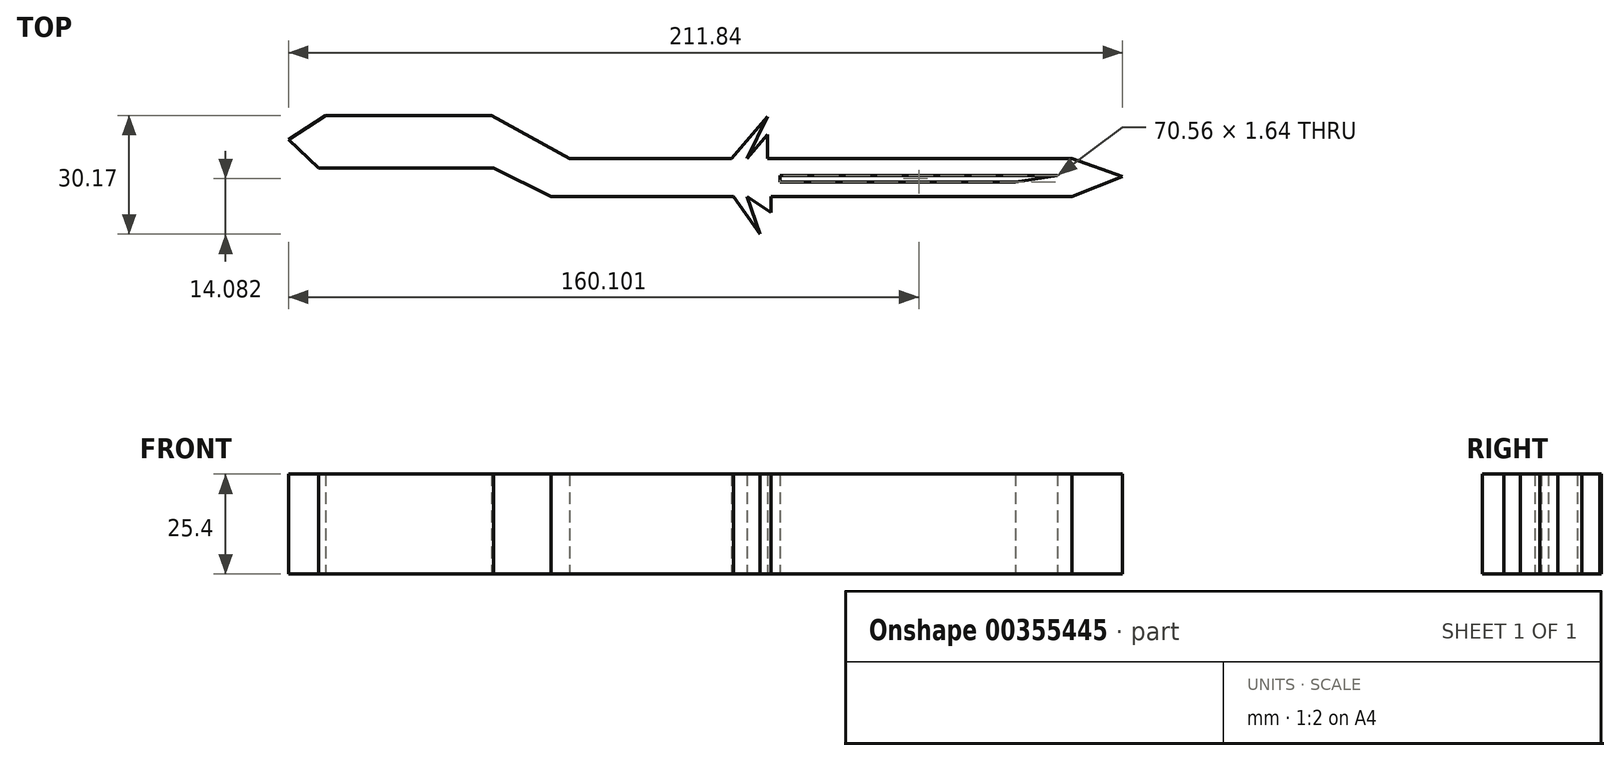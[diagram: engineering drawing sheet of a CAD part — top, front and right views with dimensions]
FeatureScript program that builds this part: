
annotation { "Feature Type Name" : "Feature", "Feature Type Description" : "" }
export const myFeature = defineFeature(function(context is Context, id is Id, definition is map)
    precondition{}
    {
        {
            var Q0;
            Q0=qCreatedBy(makeId("Top.planeOp"),FACE);
            var sketch = newSketch(context, id + "F0", { "sketchPlane" : qUnion([Q0])});
            skLineSegment(sketch, "E0", {"start": v(4.27, 9.6) * mm, "end": v(9.14, 9.6) * mm});
            skLineSegment(sketch, "E1", {"start": v(9.14, 9.6) * mm, "end": v(17.98, 9.6) * mm});
            skLineSegment(sketch, "E2", {"start": v(17.98, 9.6) * mm, "end": v(27.13, 20.27) * mm});
            skLineSegment(sketch, "E3", {"start": v(27.13, 20.27) * mm, "end": v(21.95, 9.6) * mm});
            skLineSegment(sketch, "E4", {"start": v(21.95, 9.6) * mm, "end": v(27.13, 15.65) * mm});
            skLineSegment(sketch, "E5", {"start": v(27.13, 15.65) * mm, "end": v(27.13, 9.6) * mm});
            skLineSegment(sketch, "E6", {"start": v(27.13, 9.6) * mm, "end": v(32.3, 9.6) * mm});
            skLineSegment(sketch, "E7", {"start": v(32.3, 9.6) * mm, "end": v(40.84, 9.6) * mm});
            skLineSegment(sketch, "E8", {"start": v(40.84, 9.6) * mm, "end": v(60.66, 9.6) * mm});
            skLineSegment(sketch, "E9", {"start": v(60.66, 9.6) * mm, "end": v(85.34, 9.6) * mm});
            skLineSegment(sketch, "E10", {"start": v(85.34, 9.6) * mm, "end": v(104.55, 9.6) * mm});
            skLineSegment(sketch, "E11", {"start": v(104.55, 9.6) * mm, "end": v(117.35, 5.03) * mm});
            skLineSegment(sketch, "E12", {"start": v(117.35, 5.03) * mm, "end": v(104.55, 0) * mm});
            skLineSegment(sketch, "E13", {"start": v(104.55, 0) * mm, "end": v(85.34, 0) * mm});
            skLineSegment(sketch, "E14", {"start": v(85.34, 0) * mm, "end": v(60.66, 0) * mm});
            skLineSegment(sketch, "E15", {"start": v(60.66, 0) * mm, "end": v(41.15, 0) * mm});
            skLineSegment(sketch, "E16", {"start": v(41.15, 0) * mm, "end": v(32, 0) * mm});
            skLineSegment(sketch, "E17", {"start": v(32, 0) * mm, "end": v(28.04, 0) * mm});
            skLineSegment(sketch, "E18", {"start": v(28.04, 0) * mm, "end": v(28.04, -4.11) * mm});
            skLineSegment(sketch, "E19", {"start": v(28.04, -4.11) * mm, "end": v(21.95, 0) * mm});
            skLineSegment(sketch, "E20", {"start": v(21.95, 0) * mm, "end": v(25.3, -9.6) * mm});
            skLineSegment(sketch, "E21", {"start": v(25.3, -9.6) * mm, "end": v(18.6, 0) * mm});
            skLineSegment(sketch, "E22", {"start": v(18.6, 0) * mm, "end": v(-12.2, 0) * mm});
            skLineSegment(sketch, "E23", {"start": v(-12.2, 0) * mm, "end": v(-27.74, 0) * mm});
            skLineSegment(sketch, "E24", {"start": v(-27.74, 0) * mm, "end": v(-42.37, 7.16) * mm});
            skLineSegment(sketch, "E25", {"start": v(-42.37, 7.16) * mm, "end": v(-86.87, 7.16) * mm});
            skLineSegment(sketch, "E26", {"start": v(-86.87, 7.16) * mm, "end": v(-94.49, 14.48) * mm});
            skLineSegment(sketch, "E27", {"start": v(-94.49, 14.48) * mm, "end": v(-85.04, 20.57) * mm});
            skLineSegment(sketch, "E28", {"start": v(-85.04, 20.57) * mm, "end": v(-42.98, 20.57) * mm});
            skLineSegment(sketch, "E29", {"start": v(-42.98, 20.57) * mm, "end": v(-23.16, 9.6) * mm});
            skLineSegment(sketch, "E30", {"start": v(-23.16, 9.6) * mm, "end": v(4.27, 9.6) * mm});
            skLineSegment(sketch, "E31", {"start": v(30.33, 5.3) * mm, "end": v(90.18, 5.3) * mm});
            skLineSegment(sketch, "E32", {"start": v(90.18, 5.3) * mm, "end": v(100.89, 5.3) * mm});
            skLineSegment(sketch, "E33", {"start": v(100.89, 5.3) * mm, "end": v(104.55, 9.6) * mm});
            skLineSegment(sketch, "E34", {"start": v(100.89, 5.3) * mm, "end": v(104.55, 0) * mm});
            skLineSegment(sketch, "E35", {"start": v(30.33, 5.3) * mm, "end": v(30.33, 3.66) * mm});
            skLineSegment(sketch, "E36", {"start": v(30.33, 3.66) * mm, "end": v(90.18, 3.66) * mm});
            skLineSegment(sketch, "E37", {"start": v(90.18, 3.66) * mm, "end": v(100.89, 5.3) * mm});
            skSolve(sketch);
        }
        {
            var Q0;
            Q0 = qSketchRegion(id + "F0", true);
            extrude(context, id + "F1", {"entities" : qUnion([Q0]), "depth" : 25.4 * mm});
        }
    });
